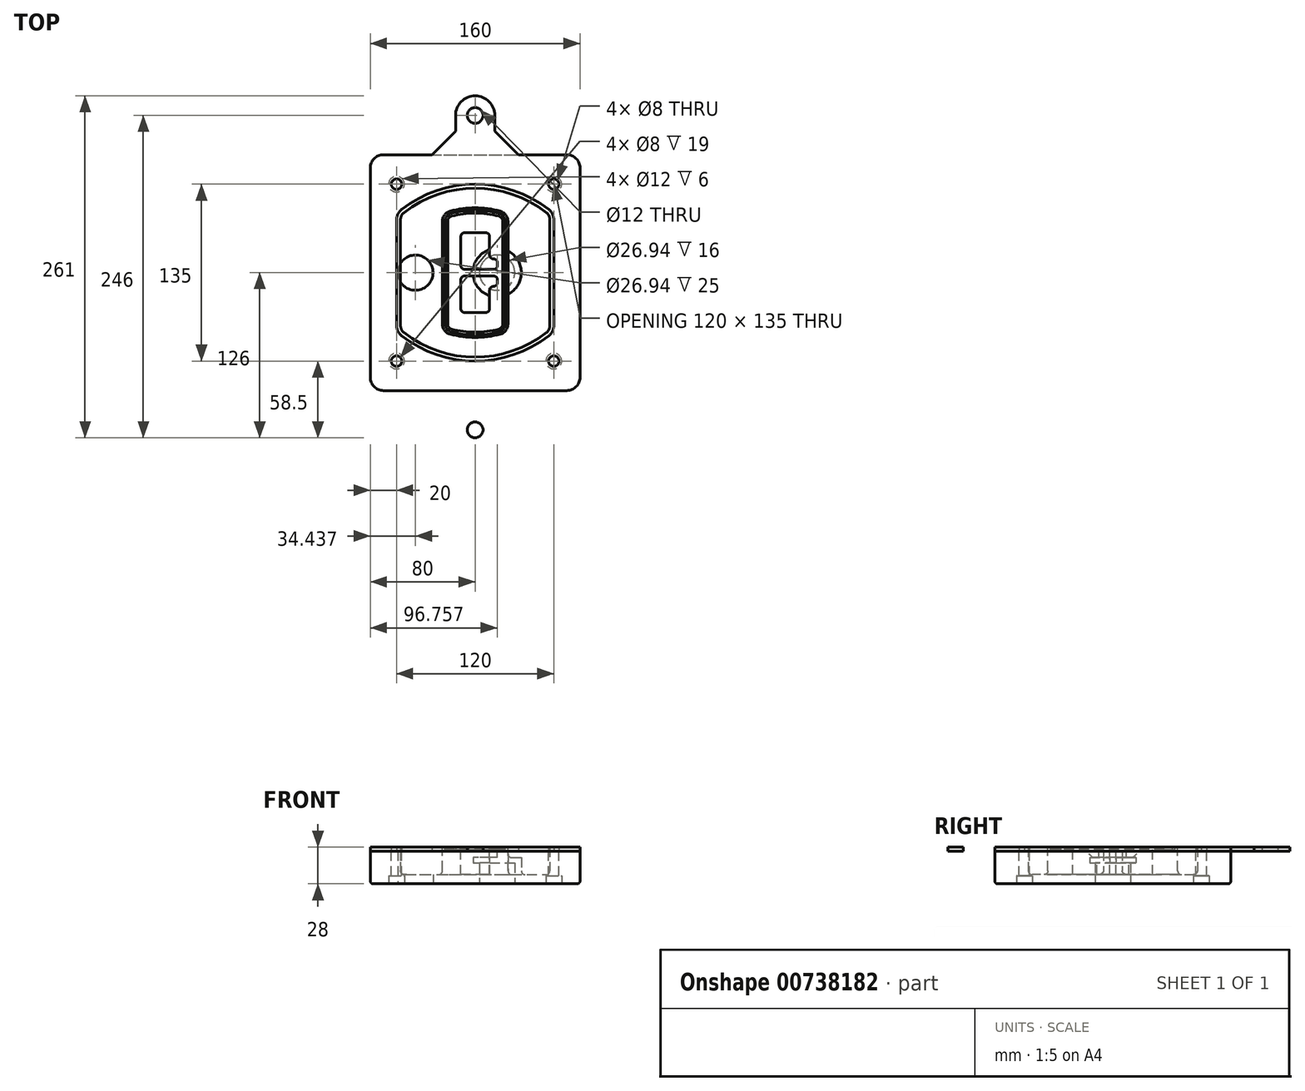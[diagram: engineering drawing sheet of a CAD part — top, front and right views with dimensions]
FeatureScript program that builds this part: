
annotation { "Feature Type Name" : "Feature", "Feature Type Description" : "" }
export const myFeature = defineFeature(function(context is Context, id is Id, definition is map)
    precondition{}
    {
        {
            var Q0;
            Q0=qCreatedBy(makeId("Top.planeOp"),FACE);
            var sketch = newSketch(context, id + "F0", { "sketchPlane" : qUnion([Q0])});
            skPoint(sketch, "E0.rect.middle", {"position": v(0, 0) * mm});
            skLineSegment(sketch, "E1.bottom", {"start": v(-70, -90) * mm, "end": v(70, -90) * mm});
            skLineSegment(sketch, "E1.top", {"start": v(-70, 90) * mm, "end": v(70, 90) * mm});
            skLineSegment(sketch, "E1.left", {"start": v(-80, -80) * mm, "end": v(-80, 80) * mm});
            skLineSegment(sketch, "E1.right", {"start": v(80, -80) * mm, "end": v(80, 80) * mm});
            skLineSegment(sketch, "E2", {"start": v(-80, 90) * mm, "end": v(80, -90) * mm, "construction": true});
            skLineSegment(sketch, "E3", {"start": v(80, 90) * mm, "end": v(-80, -90) * mm, "construction": true});
            skCircle(sketch, "E4", {"center": v(-60, 67.5) * mm, "radius": 4 * mm});
            skCircle(sketch, "E5", {"center": v(60, 67.5) * mm, "radius": 4 * mm});
            skCircle(sketch, "E6", {"center": v(60, -67.5) * mm, "radius": 4 * mm});
            skCircle(sketch, "E7", {"center": v(-60, -67.5) * mm, "radius": 4 * mm});
            skLineSegment(sketch, "E8", {"start": v(-60, 67.5) * mm, "end": v(60, 67.5) * mm, "construction": true});
            skLineSegment(sketch, "E9", {"start": v(60, 67.5) * mm, "end": v(60, -67.5) * mm, "construction": true});
            skLineSegment(sketch, "E10", {"start": v(60, -67.5) * mm, "end": v(-60, -67.5) * mm, "construction": true});
            skLineSegment(sketch, "E11", {"start": v(-60, -67.5) * mm, "end": v(-60, 67.5) * mm, "construction": true});
            skLineSegment(sketch, "E12", {"start": v(-60, 40.3) * mm, "end": v(-60, -40.3) * mm});
            skLineSegment(sketch, "E13", {"start": v(60, 40.3) * mm, "end": v(60, -40.3) * mm});
            skArc(sketch, "E14", {"start": v(56.15, 48.18) * mm, "mid": v(0, 67.5) * mm, "end": v(-56.15, 48.18) * mm});
            skArc(sketch, "E15", {"start": v(-56.15, -48.18) * mm, "mid": v(0, -67.5) * mm, "end": v(56.15, -48.18) * mm});
            skLineSegment(sketch, "E16", {"start": v(-60, 0) * mm, "end": v(60, 0) * mm, "construction": true});
            skPoint(sketch, "E17.visualSharp", {"position": v(-60, -45) * mm});
            skArc(sketch, "E17.filletArc", {"start": v(-60, -40.3) * mm, "mid": v(-58.99, -44.68) * mm, "end": v(-56.15, -48.18) * mm});
            skPoint(sketch, "E18.visualSharp", {"position": v(-60, 45) * mm});
            skArc(sketch, "E18.filletArc", {"start": v(-56.15, 48.18) * mm, "mid": v(-58.99, 44.68) * mm, "end": v(-60, 40.3) * mm});
            skPoint(sketch, "E19.visualSharp", {"position": v(60, 45) * mm});
            skArc(sketch, "E19.filletArc", {"start": v(60, 40.3) * mm, "mid": v(58.99, 44.68) * mm, "end": v(56.15, 48.18) * mm});
            skPoint(sketch, "E20.visualSharp", {"position": v(60, -45) * mm});
            skArc(sketch, "E20.filletArc", {"start": v(56.15, -48.18) * mm, "mid": v(58.99, -44.68) * mm, "end": v(60, -40.3) * mm});
            skPoint(sketch, "E21.visualSharp", {"position": v(-80, 90) * mm});
            skArc(sketch, "E21.filletArc", {"start": v(-70, 90) * mm, "mid": v(-77.07, 87.07) * mm, "end": v(-80, 80) * mm});
            skPoint(sketch, "E22.visualSharp", {"position": v(80, 90) * mm});
            skArc(sketch, "E22.filletArc", {"start": v(80, 80) * mm, "mid": v(77.07, 87.07) * mm, "end": v(70, 90) * mm});
            skPoint(sketch, "E23.visualSharp", {"position": v(80, -90) * mm});
            skArc(sketch, "E23.filletArc", {"start": v(70, -90) * mm, "mid": v(77.07, -87.07) * mm, "end": v(80, -80) * mm});
            skPoint(sketch, "E24.visualSharp", {"position": v(-80, -90) * mm});
            skArc(sketch, "E24.filletArc", {"start": v(-80, -80) * mm, "mid": v(-77.07, -87.07) * mm, "end": v(-70, -90) * mm});
            skArc(sketch, "E25.0", {"start": v(57, 40.3) * mm, "mid": v(56.3, 43.36) * mm, "end": v(54.3, 45.81) * mm});
            skLineSegment(sketch, "E25.1", {"start": v(57, 40.3) * mm, "end": v(57, -40.3) * mm});
            skArc(sketch, "E25.2", {"start": v(54.3, -45.81) * mm, "mid": v(56.3, -43.36) * mm, "end": v(57, -40.3) * mm});
            skArc(sketch, "E25.3", {"start": v(-54.3, -45.81) * mm, "mid": v(0, -64.5) * mm, "end": v(54.3, -45.81) * mm});
            skArc(sketch, "E25.4", {"start": v(-57, -40.3) * mm, "mid": v(-56.3, -43.36) * mm, "end": v(-54.3, -45.81) * mm});
            skArc(sketch, "E25.5", {"start": v(54.3, 45.81) * mm, "mid": v(0, 64.5) * mm, "end": v(-54.3, 45.81) * mm});
            skLineSegment(sketch, "E25.6", {"start": v(-57, 40.3) * mm, "end": v(-57, -40.3) * mm});
            skArc(sketch, "E25.7", {"start": v(-54.3, 45.81) * mm, "mid": v(-56.3, 43.36) * mm, "end": v(-57, 40.3) * mm});
            skArc(sketch, "E26.0", {"start": v(-58.62, 51.33) * mm, "mid": v(-62.58, 46.43) * mm, "end": v(-64, 40.3) * mm});
            skArc(sketch, "E26.1", {"start": v(58.62, 51.33) * mm, "mid": v(0, 71.5) * mm, "end": v(-58.62, 51.33) * mm});
            skArc(sketch, "E26.2", {"start": v(64, 40.3) * mm, "mid": v(62.58, 46.43) * mm, "end": v(58.62, 51.33) * mm});
            skLineSegment(sketch, "E26.3", {"start": v(64, 40.3) * mm, "end": v(64, -40.3) * mm});
            skArc(sketch, "E26.4", {"start": v(58.62, -51.33) * mm, "mid": v(62.58, -46.43) * mm, "end": v(64, -40.3) * mm});
            skLineSegment(sketch, "E26.5", {"start": v(-64, 40.3) * mm, "end": v(-64, -40.3) * mm});
            skArc(sketch, "E26.6", {"start": v(-58.62, -51.33) * mm, "mid": v(0, -71.5) * mm, "end": v(58.62, -51.33) * mm});
            skArc(sketch, "E26.7", {"start": v(-64, -40.3) * mm, "mid": v(-62.58, -46.43) * mm, "end": v(-58.62, -51.33) * mm});
            skSolve(sketch);
        }
        {
            var Q0;
            Q0=makeQuery(id+"F0.imprint","IMPRINT",FACE,{"disambiguationData":[TD([[makeQuery(id+"F0.imprint","IMPRINT",EDGE,{"derivedFrom":sQuery(id+"F0.wireOp",EDGE,"E1.bottom")}),1.0]])]});
            var Q1;
            Q1=makeQuery(id+"F0.imprint","IMPRINT",FACE,{"disambiguationData":[TD([[makeQuery(id+"F0.imprint","IMPRINT",EDGE,{"derivedFrom":sQuery(id+"F0.wireOp",EDGE,"E12")}),1.0]])]});
            var Q2;
            Q2=makeQuery(id+"F0.imprint","IMPRINT",FACE,{"disambiguationData":[TD([[makeQuery(id+"F0.imprint","IMPRINT",EDGE,{"derivedFrom":sQuery(id+"F0.wireOp",EDGE,"E25.0")}),1.0]])]});
            var Q3;
            Q3=makeQuery(id+"F0.imprint","IMPRINT",FACE,{"disambiguationData":[TD([[makeQuery(id+"F0.imprint","IMPRINT",EDGE,{"derivedFrom":sQuery(id+"F0.wireOp",EDGE,"E12")}),-1.0]])]});
            extrude(context, id + "F1", {"entities" : qUnion([Q0, Q1, Q2, Q3]), "oppositeDirection" : true, "depth" : 25 * mm});
        }
        {
            var Q0;
            Q0=makeQuery(id+"F0.imprint","IMPRINT",FACE,{"disambiguationData":[TD([[makeQuery(id+"F0.imprint","IMPRINT",EDGE,{"derivedFrom":sQuery(id+"F0.wireOp",EDGE,"E12")}),1.0]])]});
            extrude(context, id + "F2", {"entities" : qUnion([Q0]), "operationType" : NewBodyOperationType.ADD, "depth" : 3 * mm});
        }
        {
            var Q0;
            Q0=makeQuery(id+"F0.imprint","IMPRINT",FACE,{"disambiguationData":[TD([[makeQuery(id+"F0.imprint","IMPRINT",EDGE,{"derivedFrom":sQuery(id+"F0.wireOp",EDGE,"E25.0")}),1.0]])]});
            extrude(context, id + "F3", {"entities" : qUnion([Q0]), "operationType" : NewBodyOperationType.REMOVE, "oppositeDirection" : true, "depth" : 18 * mm});
        }
        {
            var Q0;
            Q0=makeQuery(id+"F2.opExtrude","CAP_FACE",FACE,{"disambiguationData":[OSD([sQuery(id+"F0.wireOp",EDGE,"E12"),sQuery(id+"F0.wireOp",EDGE,"E13"),sQuery(id+"F0.wireOp",EDGE,"E14"),sQuery(id+"F0.wireOp",EDGE,"E15"),sQuery(id+"F0.wireOp",EDGE,"E17.filletArc"),sQuery(id+"F0.wireOp",EDGE,"E18.filletArc"),sQuery(id+"F0.wireOp",EDGE,"E19.filletArc"),sQuery(id+"F0.wireOp",EDGE,"E20.filletArc"),sQuery(id+"F0.wireOp",EDGE,"E25.0"),sQuery(id+"F0.wireOp",EDGE,"E25.1"),sQuery(id+"F0.wireOp",EDGE,"E25.2"),sQuery(id+"F0.wireOp",EDGE,"E25.3"),sQuery(id+"F0.wireOp",EDGE,"E25.4"),sQuery(id+"F0.wireOp",EDGE,"E25.5"),sQuery(id+"F0.wireOp",EDGE,"E25.6"),sQuery(id+"F0.wireOp",EDGE,"E25.7")])],"isStart":false});
            var sketch = newSketch(context, id + "F4", { "sketchPlane" : qUnion([Q0])});
            skArc(sketch, "E27.0", {"start": v(-19.08, -46.97) * mm, "mid": v(0, -49.5) * mm, "end": v(19.08, -46.97) * mm});
            skArc(sketch, "E28.0", {"start": v(19.08, 46.97) * mm, "mid": v(0, 49.5) * mm, "end": v(-19.08, 46.97) * mm});
            skLineSegment(sketch, "E29", {"start": v(-25, 39.25) * mm, "end": v(-25, -39.25) * mm});
            skLineSegment(sketch, "E30", {"start": v(25, 39.25) * mm, "end": v(25, -39.25) * mm});
            skLineSegment(sketch, "E31", {"start": v(-25, 45.1) * mm, "end": v(25, 45.1) * mm, "construction": true});
            skLineSegment(sketch, "E32", {"start": v(-25, -45.1) * mm, "end": v(25, -45.1) * mm, "construction": true});
            skPoint(sketch, "E33.visualSharp", {"position": v(-25, 45.1) * mm});
            skArc(sketch, "E33.filletArc", {"start": v(-19.08, 46.97) * mm, "mid": v(-23.35, 44.11) * mm, "end": v(-25, 39.25) * mm});
            skPoint(sketch, "E34.visualSharp", {"position": v(25, 45.1) * mm});
            skArc(sketch, "E34.filletArc", {"start": v(25, 39.25) * mm, "mid": v(23.35, 44.11) * mm, "end": v(19.08, 46.97) * mm});
            skPoint(sketch, "E35.visualSharp", {"position": v(25, -45.1) * mm});
            skArc(sketch, "E35.filletArc", {"start": v(19.08, -46.97) * mm, "mid": v(23.35, -44.11) * mm, "end": v(25, -39.25) * mm});
            skPoint(sketch, "E36.visualSharp", {"position": v(-25, -45.1) * mm});
            skArc(sketch, "E36.filletArc", {"start": v(-25, -39.25) * mm, "mid": v(-23.35, -44.11) * mm, "end": v(-19.08, -46.97) * mm});
            skArc(sketch, "E37.0", {"start": v(54.3, 45.81) * mm, "mid": v(0, 64.5) * mm, "end": v(-54.3, 45.81) * mm});
            skArc(sketch, "E37.1", {"start": v(-54.3, 45.81) * mm, "mid": v(-56.3, 43.36) * mm, "end": v(-57, 40.3) * mm});
            skLineSegment(sketch, "E37.2", {"start": v(-57, 40.3) * mm, "end": v(-57, -40.3) * mm});
            skArc(sketch, "E37.3", {"start": v(-57, -40.3) * mm, "mid": v(-56.3, -43.36) * mm, "end": v(-54.3, -45.81) * mm});
            skArc(sketch, "E37.4", {"start": v(-54.3, -45.81) * mm, "mid": v(0, -64.5) * mm, "end": v(54.3, -45.81) * mm});
            skArc(sketch, "E37.5", {"start": v(54.3, -45.81) * mm, "mid": v(56.3, -43.36) * mm, "end": v(57, -40.3) * mm});
            skLineSegment(sketch, "E37.6", {"start": v(57, 40.3) * mm, "end": v(57, -40.3) * mm});
            skArc(sketch, "E37.7", {"start": v(57, 40.3) * mm, "mid": v(56.3, 43.36) * mm, "end": v(54.3, 45.81) * mm});
            skLineSegment(sketch, "E38.0", {"start": v(23, 39.25) * mm, "end": v(23, -39.25) * mm});
            skArc(sketch, "E38.1", {"start": v(18.56, -45.04) * mm, "mid": v(21.76, -42.9) * mm, "end": v(23, -39.25) * mm});
            skArc(sketch, "E38.2", {"start": v(-18.56, -45.04) * mm, "mid": v(0, -47.5) * mm, "end": v(18.56, -45.04) * mm});
            skArc(sketch, "E38.3", {"start": v(-23, -39.25) * mm, "mid": v(-21.76, -42.9) * mm, "end": v(-18.56, -45.04) * mm});
            skLineSegment(sketch, "E38.4", {"start": v(-23, 39.25) * mm, "end": v(-23, -39.25) * mm});
            skArc(sketch, "E38.5", {"start": v(23, 39.25) * mm, "mid": v(21.76, 42.9) * mm, "end": v(18.56, 45.04) * mm});
            skArc(sketch, "E38.6", {"start": v(-18.56, 45.04) * mm, "mid": v(-21.76, 42.9) * mm, "end": v(-23, 39.25) * mm});
            skArc(sketch, "E38.7", {"start": v(18.56, 45.04) * mm, "mid": v(0, 47.5) * mm, "end": v(-18.56, 45.04) * mm});
            skArc(sketch, "E39.0", {"start": v(21, 39.25) * mm, "mid": v(20.18, 41.68) * mm, "end": v(18.04, 43.1) * mm});
            skLineSegment(sketch, "E39.1", {"start": v(21, 39.25) * mm, "end": v(21, -39.25) * mm});
            skArc(sketch, "E39.2", {"start": v(18.04, -43.1) * mm, "mid": v(20.18, -41.68) * mm, "end": v(21, -39.25) * mm});
            skArc(sketch, "E39.3", {"start": v(-18.04, -43.1) * mm, "mid": v(0, -45.5) * mm, "end": v(18.04, -43.1) * mm});
            skArc(sketch, "E39.4", {"start": v(-21, -39.25) * mm, "mid": v(-20.18, -41.68) * mm, "end": v(-18.04, -43.1) * mm});
            skArc(sketch, "E39.5", {"start": v(18.04, 43.1) * mm, "mid": v(0, 45.5) * mm, "end": v(-18.04, 43.1) * mm});
            skLineSegment(sketch, "E39.6", {"start": v(-21, 39.25) * mm, "end": v(-21, -39.25) * mm});
            skArc(sketch, "E39.7", {"start": v(-18.04, 43.1) * mm, "mid": v(-20.18, 41.68) * mm, "end": v(-21, 39.25) * mm});
            skLineSegment(sketch, "E40", {"start": v(-25, 0) * mm, "end": v(25, 0) * mm, "construction": true});
            skLineSegment(sketch, "E41", {"start": v(-11, 5.5) * mm, "end": v(-11, 27.5) * mm});
            skLineSegment(sketch, "E42", {"start": v(-8, 30.5) * mm, "end": v(8, 30.5) * mm});
            skLineSegment(sketch, "E43", {"start": v(11, 27.5) * mm, "end": v(11, 13.5) * mm});
            skLineSegment(sketch, "E44", {"start": v(14, 10.5) * mm, "end": v(14, 10.5) * mm});
            skLineSegment(sketch, "E45", {"start": v(17, 7.5) * mm, "end": v(17, 5.5) * mm});
            skLineSegment(sketch, "E46", {"start": v(14, 2.5) * mm, "end": v(-8, 2.5) * mm});
            skPoint(sketch, "E47.visualSharp", {"position": v(-11, 30.5) * mm});
            skArc(sketch, "E47.filletArc", {"start": v(-8, 30.5) * mm, "mid": v(-10.12, 29.62) * mm, "end": v(-11, 27.5) * mm});
            skPoint(sketch, "E48.visualSharp", {"position": v(11, 30.5) * mm});
            skArc(sketch, "E48.filletArc", {"start": v(11, 27.5) * mm, "mid": v(10.12, 29.62) * mm, "end": v(8, 30.5) * mm});
            skPoint(sketch, "E49.visualSharp", {"position": v(11, 10.5) * mm});
            skArc(sketch, "E49.filletArc", {"start": v(11, 13.5) * mm, "mid": v(11.88, 11.38) * mm, "end": v(14, 10.5) * mm});
            skPoint(sketch, "E50.visualSharp", {"position": v(17, 10.5) * mm});
            skArc(sketch, "E50.filletArc", {"start": v(17, 7.5) * mm, "mid": v(16.12, 9.62) * mm, "end": v(14, 10.5) * mm});
            skPoint(sketch, "E51.visualSharp", {"position": v(17, 2.5) * mm});
            skArc(sketch, "E51.filletArc", {"start": v(14, 2.5) * mm, "mid": v(16.12, 3.38) * mm, "end": v(17, 5.5) * mm});
            skPoint(sketch, "E52.visualSharp", {"position": v(-11, 2.5) * mm});
            skArc(sketch, "E52.filletArc", {"start": v(-11, 5.5) * mm, "mid": v(-10.12, 3.38) * mm, "end": v(-8, 2.5) * mm});
            skLineSegment(sketch, "E53.0.MirrorCS", {"start": v(14, -2.5) * mm, "end": v(-8, -2.5) * mm});
            skArc(sketch, "E54.0.MirrorCS", {"start": v(-11, -5.5) * mm, "mid": v(-10.12, -3.38) * mm, "end": v(-8, -2.5) * mm});
            skLineSegment(sketch, "E55.0.MirrorCS", {"start": v(-11, -5.5) * mm, "end": v(-11, -27.5) * mm});
            skArc(sketch, "E56.0.MirrorCS", {"start": v(-8, -30.5) * mm, "mid": v(-10.12, -29.62) * mm, "end": v(-11, -27.5) * mm});
            skLineSegment(sketch, "E57.0.MirrorCS", {"start": v(-8, -30.5) * mm, "end": v(8, -30.5) * mm});
            skArc(sketch, "E58.0.MirrorCS", {"start": v(11, -27.5) * mm, "mid": v(10.12, -29.62) * mm, "end": v(8, -30.5) * mm});
            skLineSegment(sketch, "E59.0.MirrorCS", {"start": v(11, -27.5) * mm, "end": v(11, -13.5) * mm});
            skArc(sketch, "E60.0.MirrorCS", {"start": v(11, -13.5) * mm, "mid": v(11.88, -11.38) * mm, "end": v(14, -10.5) * mm});
            skArc(sketch, "E61.0.MirrorCS", {"start": v(17, -7.5) * mm, "mid": v(16.12, -9.62) * mm, "end": v(14, -10.5) * mm});
            skLineSegment(sketch, "E62.0.MirrorCS", {"start": v(17, -7.5) * mm, "end": v(17, -5.5) * mm});
            skArc(sketch, "E63.0.MirrorCS", {"start": v(14, -2.5) * mm, "mid": v(16.12, -3.38) * mm, "end": v(17, -5.5) * mm});
            skSolve(sketch);
        }
        {
            var Q0;
            Q0=makeQuery(id+"F4.imprint","IMPRINT",FACE,{"disambiguationData":[TD([[makeQuery(id+"F4.imprint","IMPRINT",EDGE,{"derivedFrom":sQuery(id+"F4.wireOp",EDGE,"E27.0")}),1.0]])]});
            var Q1;
            Q1=makeQuery(id+"F4.imprint","IMPRINT",FACE,{"disambiguationData":[TD([[makeQuery(id+"F4.imprint","IMPRINT",EDGE,{"derivedFrom":sQuery(id+"F4.wireOp",EDGE,"E38.0")}),-1.0]])]});
            var Q2;
            Q2=makeQuery(id+"F4.imprint","IMPRINT",FACE,{"disambiguationData":[TD([[makeQuery(id+"F4.imprint","IMPRINT",EDGE,{"derivedFrom":sQuery(id+"F4.wireOp",EDGE,"E39.0")}),1.0]])]});
            extrude(context, id + "F5", {"entities" : qUnion([Q0, Q1, Q2]), "operationType" : NewBodyOperationType.ADD, "endBound" : BoundingType.UP_TO_NEXT, "oppositeDirection" : true, "depth" : 25 * mm});
        }
        {
            var Q0;
            Q0=makeQuery(id+"F4.imprint","IMPRINT",FACE,{"disambiguationData":[TD([[makeQuery(id+"F4.imprint","IMPRINT",EDGE,{"derivedFrom":sQuery(id+"F4.wireOp",EDGE,"E38.0")}),-1.0]])]});
            extrude(context, id + "F6", {"entities" : qUnion([Q0]), "operationType" : NewBodyOperationType.REMOVE, "oppositeDirection" : true, "depth" : 2 * mm});
        }
        {
            var Q0;
            Q0=makeQuery(id+"F1.opExtrude","CAP_FACE",FACE,{"disambiguationData":[OSD([sQuery(id+"F0.wireOp",EDGE,"E1.bottom"),sQuery(id+"F0.wireOp",EDGE,"E1.top"),sQuery(id+"F0.wireOp",EDGE,"E1.left"),sQuery(id+"F0.wireOp",EDGE,"E1.right"),sQuery(id+"F0.wireOp",EDGE,"E4"),sQuery(id+"F0.wireOp",EDGE,"E5"),sQuery(id+"F0.wireOp",EDGE,"E6"),sQuery(id+"F0.wireOp",EDGE,"E7"),sQuery(id+"F0.wireOp",EDGE,"E21.filletArc"),sQuery(id+"F0.wireOp",EDGE,"E22.filletArc"),sQuery(id+"F0.wireOp",EDGE,"E23.filletArc"),sQuery(id+"F0.wireOp",EDGE,"E24.filletArc")])],"isStart":false});
            var sketch = newSketch(context, id + "F7", { "sketchPlane" : qUnion([Q0])});
            skCircle(sketch, "E64", {"center": v(16.76, 0) * mm, "radius": 13.47 * mm});
            skCircle(sketch, "E65", {"center": v(-45.56, 0) * mm, "radius": 13.47 * mm});
            skLineSegment(sketch, "E66", {"start": v(80, 0) * mm, "end": v(-80, 0) * mm});
            skCircle(sketch, "E67", {"center": v(16.76, 0) * mm, "radius": 18.47 * mm});
            skCircle(sketch, "E68", {"center": v(60, -67.5) * mm, "radius": 6 * mm});
            skCircle(sketch, "E69", {"center": v(-60, -67.5) * mm, "radius": 6 * mm});
            skCircle(sketch, "E70", {"center": v(-60, 67.5) * mm, "radius": 6 * mm});
            skCircle(sketch, "E71", {"center": v(60, 67.5) * mm, "radius": 6 * mm});
            skSolve(sketch);
        }
        {
            var Q0;
            {var subQ1=sQuery(id+"F7.wireOp",EDGE,"E66");var subQ4=sQuery(id+"F7.wireOp",EDGE,"E64");var subQ6=makeQuery(id+"F7.imprint","INTERSECT",VERTEX,{"disambiguationData":[OD(0.0)],"derivedFrom":[subQ4,subQ1]});Q0=makeQuery(id+"F7.imprint","IMPRINT",FACE,{"disambiguationData":[TD([[makeQuery(id+"F7.imprint","IMPRINT",EDGE,{"disambiguationData":[TD([[subQ6,-1.0]])],"derivedFrom":subQ4}),-1.0]])]});}
            var Q1;
            {var subQ0=sQuery(id+"F7.wireOp",EDGE,"E66");var subQ1=sQuery(id+"F7.wireOp",EDGE,"E64");var subQ3=makeQuery(id+"F7.imprint","INTERSECT",VERTEX,{"disambiguationData":[OD(0.0)],"derivedFrom":[subQ1,subQ0]});Q1=makeQuery(id+"F7.imprint","IMPRINT",FACE,{"disambiguationData":[TD([[makeQuery(id+"F7.imprint","IMPRINT",EDGE,{"disambiguationData":[TD([[subQ3,-1.0]])],"derivedFrom":subQ1}),1.0]])]});}
            var Q2;
            {var subQ0=sQuery(id+"F7.wireOp",EDGE,"E66");var subQ1=sQuery(id+"F7.wireOp",EDGE,"E64");var subQ3=makeQuery(id+"F7.imprint","INTERSECT",VERTEX,{"disambiguationData":[OD(0.0)],"derivedFrom":[subQ1,subQ0]});Q2=makeQuery(id+"F7.imprint","IMPRINT",FACE,{"disambiguationData":[TD([[makeQuery(id+"F7.imprint","IMPRINT",EDGE,{"disambiguationData":[TD([[subQ3,1.0]])],"derivedFrom":subQ1}),1.0]])]});}
            var Q3;
            {var subQ1=sQuery(id+"F7.wireOp",EDGE,"E66");var subQ4=sQuery(id+"F7.wireOp",EDGE,"E64");var subQ6=makeQuery(id+"F7.imprint","INTERSECT",VERTEX,{"disambiguationData":[OD(0.0)],"derivedFrom":[subQ4,subQ1]});Q3=makeQuery(id+"F7.imprint","IMPRINT",FACE,{"disambiguationData":[TD([[makeQuery(id+"F7.imprint","IMPRINT",EDGE,{"disambiguationData":[TD([[subQ6,1.0]])],"derivedFrom":subQ4}),-1.0]])]});}
            extrude(context, id + "F8", {"entities" : qUnion([Q0, Q1, Q2, Q3]), "operationType" : NewBodyOperationType.ADD, "oppositeDirection" : true, "depth" : 20 * mm});
        }
        {
            var Q0;
            {var subQ0=sQuery(id+"F7.wireOp",EDGE,"E66");var subQ1=sQuery(id+"F7.wireOp",EDGE,"E64");var subQ3=makeQuery(id+"F7.imprint","INTERSECT",VERTEX,{"disambiguationData":[OD(0.0)],"derivedFrom":[subQ1,subQ0]});Q0=makeQuery(id+"F7.imprint","IMPRINT",FACE,{"disambiguationData":[TD([[makeQuery(id+"F7.imprint","IMPRINT",EDGE,{"disambiguationData":[TD([[subQ3,-1.0]])],"derivedFrom":subQ1}),1.0]])]});}
            var Q1;
            {var subQ0=sQuery(id+"F7.wireOp",EDGE,"E66");var subQ1=sQuery(id+"F7.wireOp",EDGE,"E64");var subQ3=makeQuery(id+"F7.imprint","INTERSECT",VERTEX,{"disambiguationData":[OD(0.0)],"derivedFrom":[subQ1,subQ0]});Q1=makeQuery(id+"F7.imprint","IMPRINT",FACE,{"disambiguationData":[TD([[makeQuery(id+"F7.imprint","IMPRINT",EDGE,{"disambiguationData":[TD([[subQ3,1.0]])],"derivedFrom":subQ1}),1.0]])]});}
            extrude(context, id + "F9", {"entities" : qUnion([Q0, Q1]), "operationType" : NewBodyOperationType.REMOVE, "oppositeDirection" : true, "depth" : 16 * mm});
        }
        {
            var Q0;
            {var subQ0=sQuery(id+"F7.wireOp",EDGE,"E66");var subQ1=sQuery(id+"F7.wireOp",EDGE,"E65");var subQ3=makeQuery(id+"F7.imprint","INTERSECT",VERTEX,{"disambiguationData":[OD(0.0)],"derivedFrom":[subQ1,subQ0]});Q0=makeQuery(id+"F7.imprint","IMPRINT",FACE,{"disambiguationData":[TD([[makeQuery(id+"F7.imprint","IMPRINT",EDGE,{"disambiguationData":[TD([[subQ3,-1.0]])],"derivedFrom":subQ1}),1.0]])]});}
            var Q1;
            {var subQ0=sQuery(id+"F7.wireOp",EDGE,"E66");var subQ1=sQuery(id+"F7.wireOp",EDGE,"E65");var subQ3=makeQuery(id+"F7.imprint","INTERSECT",VERTEX,{"disambiguationData":[OD(0.0)],"derivedFrom":[subQ1,subQ0]});Q1=makeQuery(id+"F7.imprint","IMPRINT",FACE,{"disambiguationData":[TD([[makeQuery(id+"F7.imprint","IMPRINT",EDGE,{"disambiguationData":[TD([[subQ3,1.0]])],"derivedFrom":subQ1}),1.0]])]});}
            extrude(context, id + "F10", {"entities" : qUnion([Q0, Q1]), "operationType" : NewBodyOperationType.REMOVE, "oppositeDirection" : true, "depth" : 25 * mm});
        }
        {
            var Q0;
            Q0=makeQuery(id+"F7.imprint","IMPRINT",FACE,{"disambiguationData":[TD([[makeQuery(id+"F7.imprint","IMPRINT",EDGE,{"derivedFrom":sQuery(id+"F7.wireOp",EDGE,"E68")}),1.0]])]});
            var Q1;
            Q1=makeQuery(id+"F7.imprint","IMPRINT",FACE,{"disambiguationData":[TD([[makeQuery(id+"F7.imprint","IMPRINT",EDGE,{"derivedFrom":makeQuery(id+"F1.opExtrude","CAP_EDGE",EDGE,{"disambiguationData":[OSD([sQuery(id+"F0.wireOp",EDGE,"E5")])],"isStart":false})}),-1.0]])]});
            var Q2;
            Q2=makeQuery(id+"F7.imprint","IMPRINT",FACE,{"disambiguationData":[TD([[makeQuery(id+"F7.imprint","IMPRINT",EDGE,{"derivedFrom":sQuery(id+"F7.wireOp",EDGE,"E69")}),1.0]])]});
            var Q3;
            Q3=makeQuery(id+"F7.imprint","IMPRINT",FACE,{"disambiguationData":[TD([[makeQuery(id+"F7.imprint","IMPRINT",EDGE,{"derivedFrom":makeQuery(id+"F1.opExtrude","CAP_EDGE",EDGE,{"disambiguationData":[OSD([sQuery(id+"F0.wireOp",EDGE,"E4")])],"isStart":false})}),-1.0]])]});
            var Q4;
            Q4=makeQuery(id+"F7.imprint","IMPRINT",FACE,{"disambiguationData":[TD([[makeQuery(id+"F7.imprint","IMPRINT",EDGE,{"derivedFrom":sQuery(id+"F7.wireOp",EDGE,"E70")}),1.0]])]});
            var Q5;
            Q5=makeQuery(id+"F7.imprint","IMPRINT",FACE,{"disambiguationData":[TD([[makeQuery(id+"F7.imprint","IMPRINT",EDGE,{"derivedFrom":makeQuery(id+"F1.opExtrude","CAP_EDGE",EDGE,{"disambiguationData":[OSD([sQuery(id+"F0.wireOp",EDGE,"E7")])],"isStart":false})}),-1.0]])]});
            var Q6;
            Q6=makeQuery(id+"F7.imprint","IMPRINT",FACE,{"disambiguationData":[TD([[makeQuery(id+"F7.imprint","IMPRINT",EDGE,{"derivedFrom":sQuery(id+"F7.wireOp",EDGE,"E71")}),1.0]])]});
            var Q7;
            Q7=makeQuery(id+"F7.imprint","IMPRINT",FACE,{"disambiguationData":[TD([[makeQuery(id+"F7.imprint","IMPRINT",EDGE,{"derivedFrom":makeQuery(id+"F1.opExtrude","CAP_EDGE",EDGE,{"disambiguationData":[OSD([sQuery(id+"F0.wireOp",EDGE,"E6")])],"isStart":false})}),-1.0]])]});
            extrude(context, id + "F11", {"entities" : qUnion([Q0, Q1, Q2, Q3, Q4, Q5, Q6, Q7]), "operationType" : NewBodyOperationType.REMOVE, "oppositeDirection" : true, "depth" : 6 * mm});
        }
        {
            var Q0;
            Q0=makeQuery(id+"F9.boolean.opBoolean","COPY",FACE,{"derivedFrom":makeQuery(id+"F9.opExtrude","CAP_FACE",FACE,{"disambiguationData":[OSD([sQuery(id+"F7.wireOp",EDGE,"E64")])],"isStart":false})});
            var sketch = newSketch(context, id + "F12", { "sketchPlane" : qUnion([Q0])});
            skArc(sketch, "E72.0", {"start": v(11, 17.55) * mm, "mid": v(2.57, 11.82) * mm, "end": v(-1.54, 2.5) * mm});
            skArc(sketch, "E72.1", {"start": v(-1.54, -2.5) * mm, "mid": v(2.57, -11.82) * mm, "end": v(11, -17.55) * mm});
            skLineSegment(sketch, "E73", {"start": v(-1.54, -2.5) * mm, "end": v(14, -2.5) * mm});
            skLineSegment(sketch, "E74.0", {"start": v(14, 2.5) * mm, "end": v(-1.54, 2.5) * mm});
            skArc(sketch, "E74.1", {"start": v(14, 2.5) * mm, "mid": v(16.12, 3.38) * mm, "end": v(17, 5.5) * mm});
            skLineSegment(sketch, "E74.2", {"start": v(17, 7.5) * mm, "end": v(17, 5.5) * mm});
            skArc(sketch, "E74.3", {"start": v(17, 7.5) * mm, "mid": v(16.12, 9.62) * mm, "end": v(14, 10.5) * mm});
            skArc(sketch, "E74.4", {"start": v(11, 13.5) * mm, "mid": v(11.88, 11.38) * mm, "end": v(14, 10.5) * mm});
            skLineSegment(sketch, "E74.5", {"start": v(11, 17.55) * mm, "end": v(11, 13.5) * mm});
            skLineSegment(sketch, "E74.7", {"start": v(14, -2.5) * mm, "end": v(-1.54, -2.5) * mm});
            skArc(sketch, "E74.8", {"start": v(14, -2.5) * mm, "mid": v(16.12, -3.38) * mm, "end": v(17, -5.5) * mm});
            skLineSegment(sketch, "E74.9", {"start": v(17, -7.5) * mm, "end": v(17, -5.5) * mm});
            skArc(sketch, "E74.10", {"start": v(17, -7.5) * mm, "mid": v(16.12, -9.62) * mm, "end": v(14, -10.5) * mm});
            skArc(sketch, "E74.11", {"start": v(11, -13.5) * mm, "mid": v(11.88, -11.38) * mm, "end": v(14, -10.5) * mm});
            skLineSegment(sketch, "E74.12", {"start": v(11, -17.55) * mm, "end": v(11, -13.5) * mm});
            skPoint(sketch, "E75.orphan", {"position": v(11, -27.5) * mm});
            skPoint(sketch, "E76.orphan", {"position": v(-8, -2.5) * mm});
            skPoint(sketch, "E77.orphan", {"position": v(-8, 2.5) * mm});
            skPoint(sketch, "E78.orphan", {"position": v(11, 27.5) * mm});
            skSolve(sketch);
        }
        {
            var Q0;
            {var subQ7=sQuery(id+"F12.wireOp",EDGE,"E72.0");var subQ14=sQuery(id+"F12.wireOp",EDGE,"E72.1");var subQ16=sQuery(id+"F12.wireOp",EDGE,"E74.1");var subQ18=sQuery(id+"F12.wireOp",EDGE,"E74.8");Q0=qUnion([makeQuery(id+"F12.imprint","IMPRINT",FACE,{"disambiguationData":[TD([[makeQuery(id+"F12.imprint","IMPRINT",EDGE,{"derivedFrom":subQ7}),1.0]])]}),makeQuery(id+"F12.imprint","IMPRINT",FACE,{"disambiguationData":[TD([[makeQuery(id+"F12.imprint","IMPRINT",EDGE,{"derivedFrom":subQ14}),1.0]])]}),makeQuery(id+"F12.imprint","IMPRINT",FACE,{"disambiguationData":[TD([[makeQuery(id+"F12.imprint","IMPRINT",EDGE,{"derivedFrom":subQ16}),1.0]])]}),makeQuery(id+"F12.imprint","IMPRINT",FACE,{"disambiguationData":[TD([[makeQuery(id+"F12.imprint","IMPRINT",EDGE,{"derivedFrom":subQ18}),-1.0]])]})]);}
            var Q1;
            Q1=makeQuery(id+"F5.boolean.opBoolean","SPLIT",FACE,{"disambiguationData":[TD([makeQuery(id+"F5.opExtrude","SWEPT_FACE",FACE,{"disambiguationData":[OSD([sQuery(id+"F4.wireOp",EDGE,"E41")])]})])],"derivedFrom":makeQuery(id+"F3.boolean.opBoolean","COPY",FACE,{"derivedFrom":makeQuery(id+"F3.opExtrude","CAP_FACE",FACE,{"disambiguationData":[OSD([sQuery(id+"F0.wireOp",EDGE,"E25.0"),sQuery(id+"F0.wireOp",EDGE,"E25.1"),sQuery(id+"F0.wireOp",EDGE,"E25.2"),sQuery(id+"F0.wireOp",EDGE,"E25.3"),sQuery(id+"F0.wireOp",EDGE,"E25.4"),sQuery(id+"F0.wireOp",EDGE,"E25.5"),sQuery(id+"F0.wireOp",EDGE,"E25.6"),sQuery(id+"F0.wireOp",EDGE,"E25.7")])],"isStart":false})})});
            extrude(context, id + "F13", {"entities" : qUnion([Q0]), "operationType" : NewBodyOperationType.REMOVE, "endBound" : BoundingType.UP_TO_SURFACE, "endBoundEntityFace" : qUnion([Q1]), "depth" : 25 * mm});
        }
        {
            var Q0;
            Q0=makeQuery(id+"F3.boolean.opBoolean","COPY",EDGE,{"derivedFrom":makeQuery(id+"F3.opExtrude","CAP_EDGE",EDGE,{"disambiguationData":[OSD([sQuery(id+"F0.wireOp",EDGE,"E25.6")])],"isStart":false})});
            var Q1;
            Q1=makeQuery(id+"F8.boolean.opBoolean","INTERSECT",EDGE,{"derivedFrom":[makeQuery(id+"F5.opExtrude","SWEPT_FACE",FACE,{"disambiguationData":[OSD([sQuery(id+"F4.wireOp",EDGE,"E30")])]}),makeQuery(id+"F8.opExtrude","CAP_FACE",FACE,{"disambiguationData":[OSD([sQuery(id+"F7.wireOp",EDGE,"E67")])],"isStart":false})]});
            var Q2;
            Q2=makeQuery(id+"F8.boolean.opBoolean","INTERSECT",EDGE,{"disambiguationData":[OD(1.0)],"derivedFrom":[makeQuery(id+"F5.opExtrude","SWEPT_FACE",FACE,{"disambiguationData":[OSD([sQuery(id+"F4.wireOp",EDGE,"E30")])]}),makeQuery(id+"F8.opExtrude","SWEPT_FACE",FACE,{"disambiguationData":[OSD([sQuery(id+"F7.wireOp",EDGE,"E67")])]})]});
            var Q3;
            {var subQ0=sQuery(id+"F4.wireOp",EDGE,"E30");Q3=makeQuery(id+"F8.boolean.opBoolean","SPLIT",EDGE,{"disambiguationData":[TD([makeQuery(id+"F5.opExtrude","SWEPT_FACE",FACE,{"disambiguationData":[OSD([sQuery(id+"F4.wireOp",EDGE,"E35.filletArc")])]})])],"derivedFrom":makeQuery(id+"F5.opExtrude","CAP_EDGE",EDGE,{"disambiguationData":[OSD([subQ0])],"isStart":false})});}
            var Q4;
            {var subQ0=sQuery(id+"F0.wireOp",EDGE,"E25.7");var subQ1=sQuery(id+"F0.wireOp",EDGE,"E25.1");var subQ2=sQuery(id+"F0.wireOp",EDGE,"E25.6");var subQ3=sQuery(id+"F0.wireOp",EDGE,"E25.5");var subQ4=sQuery(id+"F0.wireOp",EDGE,"E25.4");var subQ5=sQuery(id+"F0.wireOp",EDGE,"E25.0");var subQ6=sQuery(id+"F0.wireOp",EDGE,"E25.2");var subQ7=sQuery(id+"F0.wireOp",EDGE,"E25.3");Q4=makeQuery(id+"F8.boolean.opBoolean","INTERSECT",EDGE,{"derivedFrom":[makeQuery(id+"F5.boolean.opBoolean","SPLIT",FACE,{"disambiguationData":[TD([makeQuery(id+"F2.opExtrude","SWEPT_FACE",FACE,{"disambiguationData":[OSD([subQ5])]})])],"derivedFrom":makeQuery(id+"F3.boolean.opBoolean","COPY",FACE,{"derivedFrom":makeQuery(id+"F3.opExtrude","CAP_FACE",FACE,{"disambiguationData":[OSD([subQ5,subQ1,subQ6,subQ7,subQ4,subQ3,subQ2,subQ0])],"isStart":false})})}),makeQuery(id+"F8.opExtrude","SWEPT_FACE",FACE,{"disambiguationData":[OSD([sQuery(id+"F7.wireOp",EDGE,"E67")])]})]});}
            var Q5;
            Q5=makeQuery(id+"F8.boolean.opBoolean","INTERSECT",EDGE,{"disambiguationData":[OD(0.0)],"derivedFrom":[makeQuery(id+"F5.opExtrude","SWEPT_FACE",FACE,{"disambiguationData":[OSD([sQuery(id+"F4.wireOp",EDGE,"E30")])]}),makeQuery(id+"F8.opExtrude","SWEPT_FACE",FACE,{"disambiguationData":[OSD([sQuery(id+"F7.wireOp",EDGE,"E67")])]})]});
            fillet(context, id + "F14", {"entities" : qUnion([Q0, Q1, Q2, Q3, Q4, Q5]), "radius" : 3 * mm, "tangentPropagation" : true, "allowEdgeOverflow" : false});
        }
        {
            var Q0;
            Q0=makeQuery(id+"F1.opExtrude","CAP_EDGE",EDGE,{"disambiguationData":[OSD([sQuery(id+"F0.wireOp",EDGE,"E1.bottom")])],"isStart":false});
            fillet(context, id + "F15", {"entities" : qUnion([Q0]), "radius" : 2 * mm, "tangentPropagation" : true, "allowEdgeOverflow" : false});
        }
        {
            var Q0;
            {var subQ0=sQuery(id+"F0.wireOp",EDGE,"E21.filletArc");var subQ1=sQuery(id+"F0.wireOp",EDGE,"E7");var subQ2=sQuery(id+"F0.wireOp",EDGE,"E6");var subQ3=sQuery(id+"F0.wireOp",EDGE,"E5");var subQ4=sQuery(id+"F0.wireOp",EDGE,"E4");var subQ5=sQuery(id+"F0.wireOp",EDGE,"E22.filletArc");var subQ6=sQuery(id+"F0.wireOp",EDGE,"E1.bottom");var subQ7=sQuery(id+"F0.wireOp",EDGE,"E1.right");var subQ8=sQuery(id+"F0.wireOp",EDGE,"E1.top");var subQ9=sQuery(id+"F0.wireOp",EDGE,"E1.left");var subQ10=sQuery(id+"F0.wireOp",EDGE,"E23.filletArc");var subQ11=sQuery(id+"F0.wireOp",EDGE,"E24.filletArc");Q0=makeQuery(id+"F2.boolean.opBoolean","SPLIT",FACE,{"disambiguationData":[TD([makeQuery(id+"F1.opExtrude","SWEPT_FACE",FACE,{"disambiguationData":[OSD([subQ6])]})])],"derivedFrom":makeQuery(id+"F1.opExtrude","CAP_FACE",FACE,{"disambiguationData":[OSD([subQ6,subQ8,subQ9,subQ7,subQ4,subQ3,subQ2,subQ1,subQ0,subQ5,subQ10,subQ11])],"isStart":true})});}
            var sketch = newSketch(context, id + "F16", { "sketchPlane" : qUnion([Q0])});
            skLineSegment(sketch, "E79", {"start": v(-15, 108) * mm, "end": v(-15, 120) * mm});
            skLineSegment(sketch, "E80", {"start": v(15, 108) * mm, "end": v(15, 120) * mm});
            skLineSegment(sketch, "E81", {"start": v(-80, 0) * mm, "end": v(80, 0) * mm, "construction": true});
            skLineSegment(sketch, "E82", {"start": v(0, 90) * mm, "end": v(0, 120) * mm, "construction": true});
            skCircle(sketch, "E83", {"center": v(0, 120) * mm, "radius": 6 * mm});
            skArc(sketch, "E84", {"start": v(-15, 120) * mm, "mid": v(0, 135) * mm, "end": v(15, 120) * mm});
            skLineSegment(sketch, "E85.0", {"start": v(-70, 90) * mm, "end": v(70, 90) * mm});
            skLineSegment(sketch, "E86", {"start": v(-15, 108) * mm, "end": v(-33, 90) * mm});
            skLineSegment(sketch, "E87", {"start": v(15, 108) * mm, "end": v(33, 90) * mm});
            skLineSegment(sketch, "E88.0", {"start": v(-70, -90) * mm, "end": v(70, -90) * mm});
            skCircle(sketch, "E89.MirrorC", {"center": v(0, -120) * mm, "radius": 6 * mm});
            skLineSegment(sketch, "E90.MirrorCS", {"start": v(15, -108) * mm, "end": v(15, -120) * mm});
            skLineSegment(sketch, "E91.MirrorCS", {"start": v(-15, -108) * mm, "end": v(-15, -120) * mm});
            skLineSegment(sketch, "E92.MirrorCS", {"start": v(15, -108) * mm, "end": v(33, -90) * mm});
            skLineSegment(sketch, "E93.MirrorCS", {"start": v(-15, -108) * mm, "end": v(-33, -90) * mm});
            skArc(sketch, "E94.MirrorCS", {"start": v(-15, -120) * mm, "mid": v(0, -135) * mm, "end": v(15, -120) * mm});
            skLineSegment(sketch, "E95.MirrorCS", {"start": v(0, -90) * mm, "end": v(0, -120) * mm, "construction": true});
            skSolve(sketch);
        }
        {
            var Q0;
            Q0=makeQuery(id+"F16.imprint","IMPRINT",FACE,{"disambiguationData":[TD([[makeQuery(id+"F16.imprint","IMPRINT",EDGE,{"derivedFrom":sQuery(id+"F16.wireOp",EDGE,"E89.MirrorC")}),1.0]])]});
            var Q1;
            Q1=makeQuery(id+"F16.imprint","IMPRINT",FACE,{"disambiguationData":[TD([[makeQuery(id+"F16.imprint","IMPRINT",EDGE,{"derivedFrom":makeQuery(id+"F1.opExtrude","CAP_EDGE",EDGE,{"disambiguationData":[OSD([sQuery(id+"F0.wireOp",EDGE,"E1.left")])],"isStart":true})}),-1.0]])]});
            var Q2;
            Q2=makeQuery(id+"F16.imprint","IMPRINT",FACE,{"disambiguationData":[TD([[makeQuery(id+"F16.imprint","IMPRINT",EDGE,{"derivedFrom":sQuery(id+"F16.wireOp",EDGE,"E79")}),-1.0]])]});
            var Q3;
            Q3=makeQuery(id+"F2.opExtrude","CAP_FACE",FACE,{"disambiguationData":[OSD([sQuery(id+"F0.wireOp",EDGE,"E12"),sQuery(id+"F0.wireOp",EDGE,"E13"),sQuery(id+"F0.wireOp",EDGE,"E14"),sQuery(id+"F0.wireOp",EDGE,"E15"),sQuery(id+"F0.wireOp",EDGE,"E17.filletArc"),sQuery(id+"F0.wireOp",EDGE,"E18.filletArc"),sQuery(id+"F0.wireOp",EDGE,"E19.filletArc"),sQuery(id+"F0.wireOp",EDGE,"E20.filletArc"),sQuery(id+"F0.wireOp",EDGE,"E25.0"),sQuery(id+"F0.wireOp",EDGE,"E25.1"),sQuery(id+"F0.wireOp",EDGE,"E25.2"),sQuery(id+"F0.wireOp",EDGE,"E25.3"),sQuery(id+"F0.wireOp",EDGE,"E25.4"),sQuery(id+"F0.wireOp",EDGE,"E25.5"),sQuery(id+"F0.wireOp",EDGE,"E25.6"),sQuery(id+"F0.wireOp",EDGE,"E25.7")])],"isStart":false});
            extrude(context, id + "F17", {"entities" : qUnion([Q0, Q1, Q2]), "endBound" : BoundingType.UP_TO_SURFACE, "depth" : 25 * mm, "endBoundEntityFace" : qUnion([Q3]), "offsetDistance" : 25 * mm});
        }
    });
